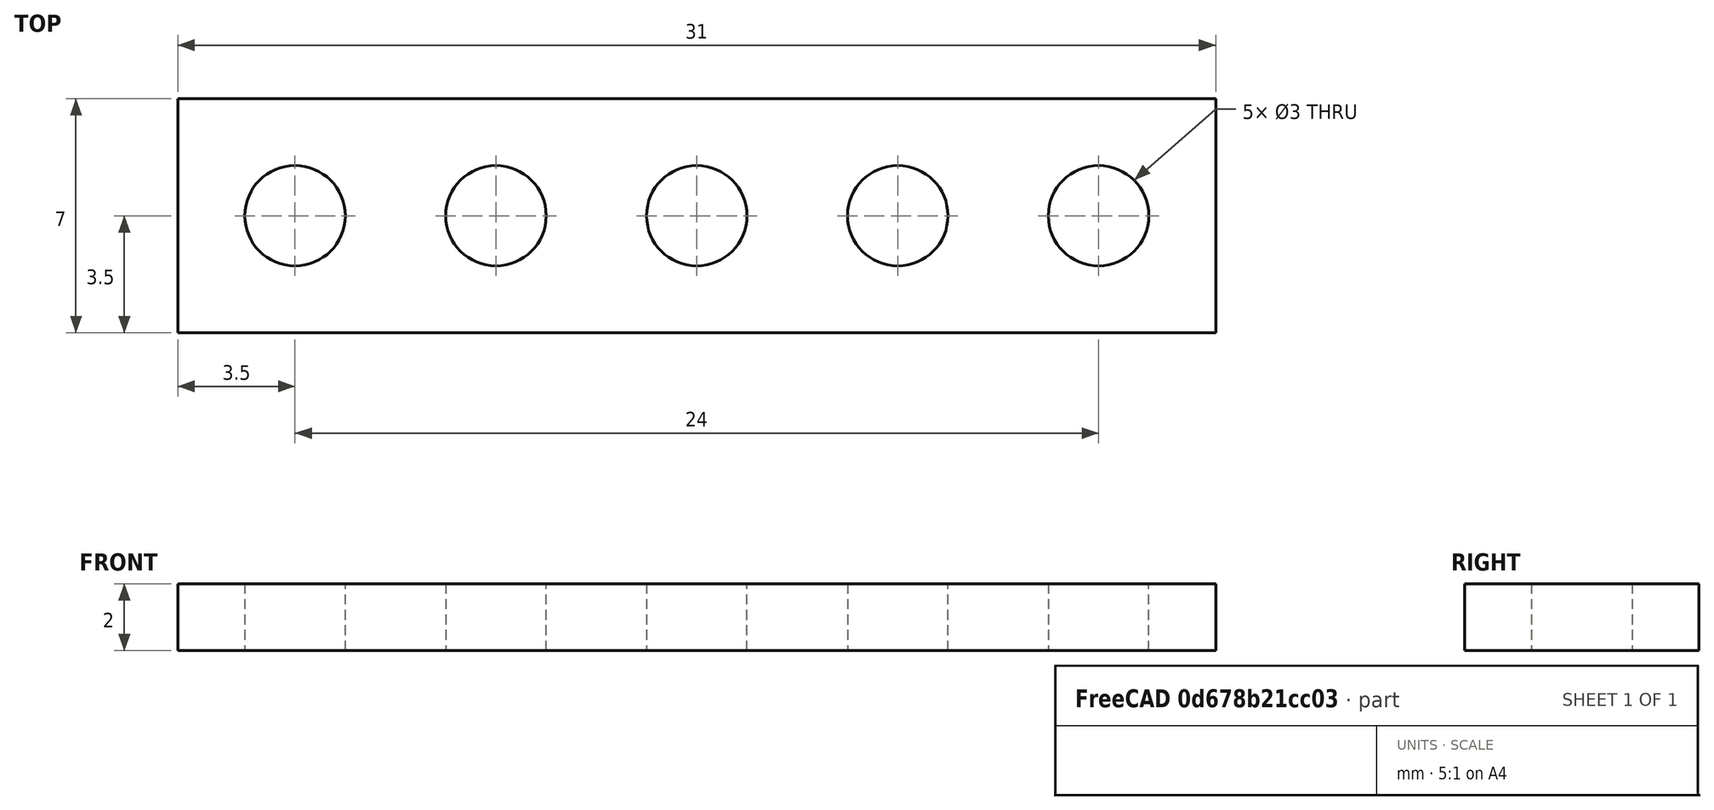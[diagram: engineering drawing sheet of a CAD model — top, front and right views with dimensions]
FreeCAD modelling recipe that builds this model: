
FCSTD DOCUMENT  (FreeCAD 0.21R33694 (Git))
Label: OJT1_T10R01_pieza_5_forats
License: All rights reserved
LicenseURL: http://en.wikipedia.org/wiki/All_rights_reserved
objects: Part::Cylinder×5, Part::Cut×5, Part::Box×1
note: 11 computed .brp shape members not serialized (recipe doc carries the construction recipe); baked Part::Feature solids carry a one-line shape summary decoded from their .brp

FEATURE [Part::Box] Box  label="Cube"
  AttacherType = Attacher::AttachEngine3D
  Height = 2
  Length = 31
  Width = 7
FEATURE [Part::Cylinder] Cylinder
  Angle = 360
  AttacherType = Attacher::AttachEngine3D
  FirstAngle = 0
  Height = 2
  Placement = pos=(3.5,3.5,0) rot=(0,0,1;0rad)
  Radius = 1.5
  SecondAngle = 0
FEATURE [Part::Cylinder] Cylinder001
  Angle = 360
  AttacherType = Attacher::AttachEngine3D
  FirstAngle = 0
  Height = 2
  Placement = pos=(27.5,3.5,0) rot=(0,0,1;0rad)
  Radius = 1.5
  SecondAngle = 0
FEATURE [Part::Cylinder] Cylinder002
  Angle = 360
  AttacherType = Attacher::AttachEngine3D
  FirstAngle = 0
  Height = 2
  Placement = pos=(15.5,3.5,0) rot=(0,0,1;0rad)
  Radius = 1.5
  SecondAngle = 0
FEATURE [Part::Cylinder] Cylinder003
  Angle = 360
  AttacherType = Attacher::AttachEngine3D
  FirstAngle = 0
  Height = 2
  Placement = pos=(21.5,3.5,0) rot=(0,0,1;0rad)
  Radius = 1.5
  SecondAngle = 0
FEATURE [Part::Cylinder] Cylinder004
  Angle = 360
  AttacherType = Attacher::AttachEngine3D
  FirstAngle = 0
  Height = 2
  Placement = pos=(9.5,3.5,0) rot=(0,0,1;0rad)
  Radius = 1.5
  SecondAngle = 0
FEATURE [Part::Cut] Cut
  Base = -> Box
  Refine = true
  Tool = -> Cylinder
FEATURE [Part::Cut] Cut001
  Base = -> Cut
  Refine = true
  Tool = -> Cylinder001
FEATURE [Part::Cut] Cut002
  Base = -> Cut001
  Refine = true
  Tool = -> Cylinder004
FEATURE [Part::Cut] Cut003
  Base = -> Cut002
  Refine = true
  Tool = -> Cylinder003
FEATURE [Part::Cut] Cut004
  Base = -> Cut003
  Refine = true
  Tool = -> Cylinder002
